# Revit family: LCV-CM
name_source: partatom
category: Lighting Fixtures
revit_build: Autodesk Revit 2013 (Build: 20130531_2115(x64)
units: mm (PartAtom-declared; Revit-internal decimal feet)

## types (5) — shared parameters
Color Filter = 16777215
Default Elevation = 48"
Description = A beautiful curved shape with low maintenance, high performance LED.
Dimming Lamp Color Temperature Shift = <None>
Emit Shape Visible in Rendering = No
Emit from Rectangle Length = 46"
Emit from Rectangle Width = 7"
Glass = Hubbell - White Glass
Housing Material = Hubbell - White
Lamp = LED
Load Classification = Lighting
Manufacturer = Alera Lighting
Model = LCV
Photometric Notes = More IES files download on Photometric Web Link
Photometric Web Link = https://www.hubbell.com
Power Factor = 1
Product Documentation Link = https://hubbellcdn.com
Product Page URL = https://www.hubbell.com
Row Length = 48"
Suspension Height = 24"
Tilt Angle = -90.00°
URL = https://www.hubbell.com
Voltage = 120 V
Wattage Comments = 27W to 61W

## per-type parameters (varying)
| type | Apparent Load | LED Lumen | Photometric Web File | Watts |
| LCV-35VL-SQP | 61 VA | Very High Lumen | LCV-35VL-SQP.IES | 61 W |
| LCV-35LW-PERF | 38 VA | Low Watt | LCV-35LW-PERF.IES | 38 W |
| LCV-35ML-S | 47 VA | Medium Lumen | LCV-35ML-S.IES | 47 W |
| LCV-40VW-S | 27 VA | Very Low Watt | LCV-40VW-S.IES | 27 W |
| LCV-35HL-PERF | 57 VA | High Lumen | LCV-35HL-PERF.IES | 57 W |

## geometry (parser evidence)
native form markers: Blend x8, Sweep x4
no freeform markers — native parametric forms only
